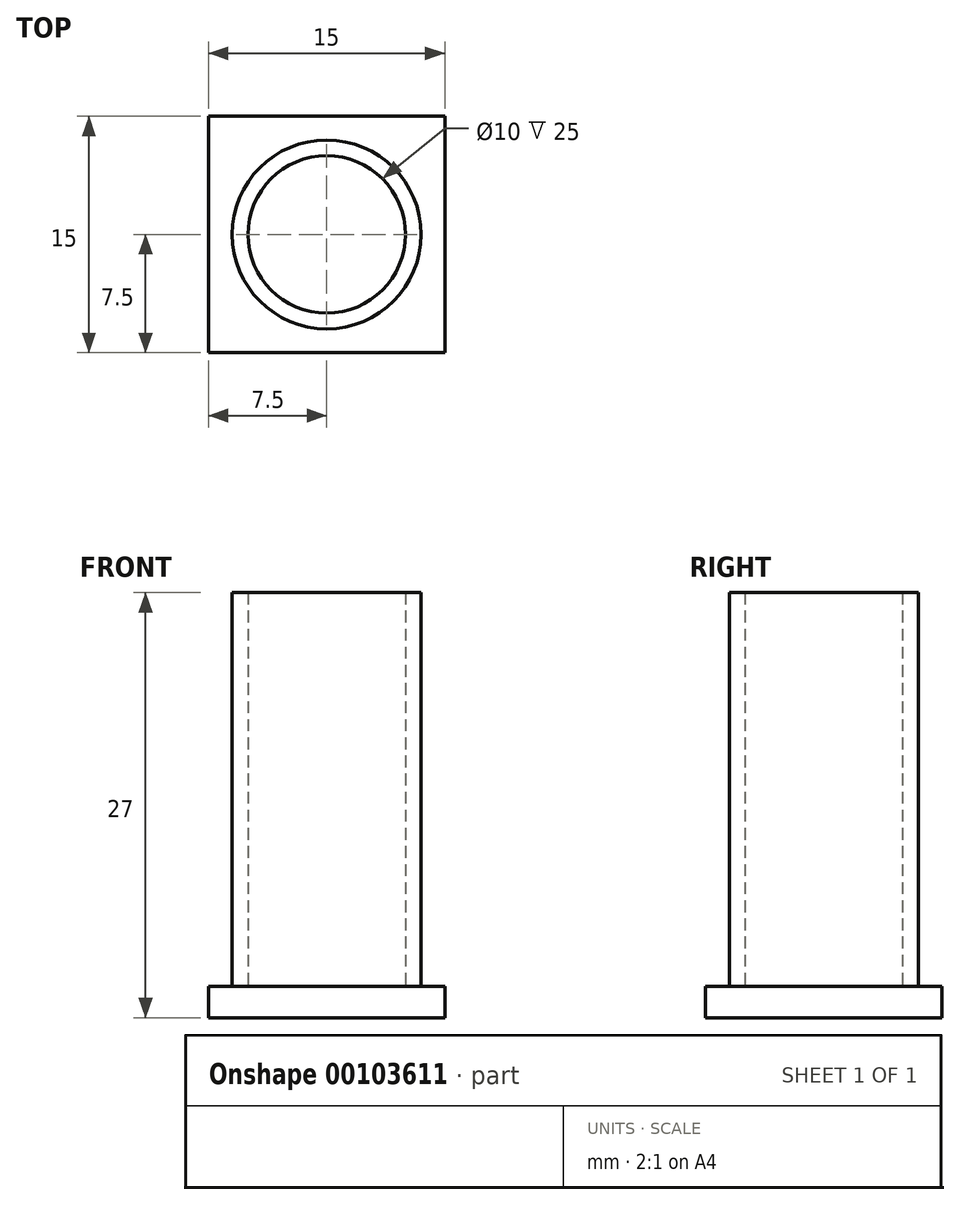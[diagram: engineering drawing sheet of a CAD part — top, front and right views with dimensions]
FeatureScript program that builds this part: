
annotation { "Feature Type Name" : "Feature", "Feature Type Description" : "" }
export const myFeature = defineFeature(function(context is Context, id is Id, definition is map)
    precondition{}
    {
        {
            var Q0;
            Q0=qCreatedBy(makeId("Top.planeOp"),FACE);
            var sketch = newSketch(context, id + "F0", { "sketchPlane" : qUnion([Q0])});
            skLineSegment(sketch, "E0.bottom", {"start": v(7.5, 7.5) * mm, "end": v(-7.5, 7.5) * mm});
            skLineSegment(sketch, "E0.top", {"start": v(7.5, -7.5) * mm, "end": v(-7.5, -7.5) * mm});
            skLineSegment(sketch, "E0.left", {"start": v(7.5, 7.5) * mm, "end": v(7.5, -7.5) * mm});
            skLineSegment(sketch, "E0.right", {"start": v(-7.5, 7.5) * mm, "end": v(-7.5, -7.5) * mm});
            skPoint(sketch, "E0.middle", {"position": v(0, 0) * mm});
            skSolve(sketch);
        }
        {
            var Q0;
            Q0 = qSketchRegion(id + "F0", true);
            extrude(context, id + "F1", {"entities" : qUnion([Q0]), "depth" : 2 * mm});
        }
        {
            var Q0;
            Q0=makeQuery(id+"F1.opExtrude","CAP_FACE",FACE,{"disambiguationData":[OSD([sQuery(id+"F0.wireOp",EDGE,"E0.bottom"),sQuery(id+"F0.wireOp",EDGE,"E0.top"),sQuery(id+"F0.wireOp",EDGE,"E0.left"),sQuery(id+"F0.wireOp",EDGE,"E0.right")])],"isStart":false});
            var sketch = newSketch(context, id + "F2", { "sketchPlane" : qUnion([Q0])});
            skCircle(sketch, "E1", {"center": v(0, 0) * mm, "radius": 5 * mm});
            skCircle(sketch, "E2", {"center": v(0, 0) * mm, "radius": 6 * mm});
            skSolve(sketch);
        }
        {
            var Q0;
            Q0 = qSketchRegion(id + "F2", true);
            extrude(context, id + "F3", {"entities" : qUnion([Q0]), "operationType" : NewBodyOperationType.ADD, "depth" : 25 * mm});
        }
    });
